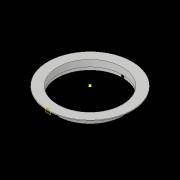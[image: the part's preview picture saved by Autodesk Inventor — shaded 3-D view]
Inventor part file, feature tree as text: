
AUTODESK INVENTOR PART (.ipt)
format: ipt  version: 2017 (Build 210142000, 142)  size: 136,192 bytes
history: native  units: in
note: dims shown in document units (in); Inventor stores cm internally (conversion verified against a paired STEP export)
features: sketch x3, revolve x1, plane x1, extrude x1
ambient origin geometry x8: Origin, YZ Plane, XZ Plane, XY Plane, X Axis, Y Axis, Z Axis, Center Point
bodies: Solid1 (feature_tree)
feature tree (6):
  revolve  "Revolution1"  [1 undecoded]
  plane  "Work Plane1"
  extrude  "Extrusion1"  Depth=0.125in
  sketch  "Sketch3"  dims[d4=0.125in d5=2.25in d6=1.5in d7=0.125in d8=90.0deg d9=0.5in d10=1.0285in d11=1.0in d12=0.0in d13=1.0285in d14=0.0625in d15=0.25in d16=0.25in]
  sketch  "Sketch1"  dims[d0=2.0in d1=5.4375in]
  sketch  "Sketch2"  dims[d2=1.25in d3=0.125in]
note: 1 required parameter value undecoded (feature->parameter linkage not recoverable at this tier; creation-order binding heuristic only, values carry confidence <= 0.55)
